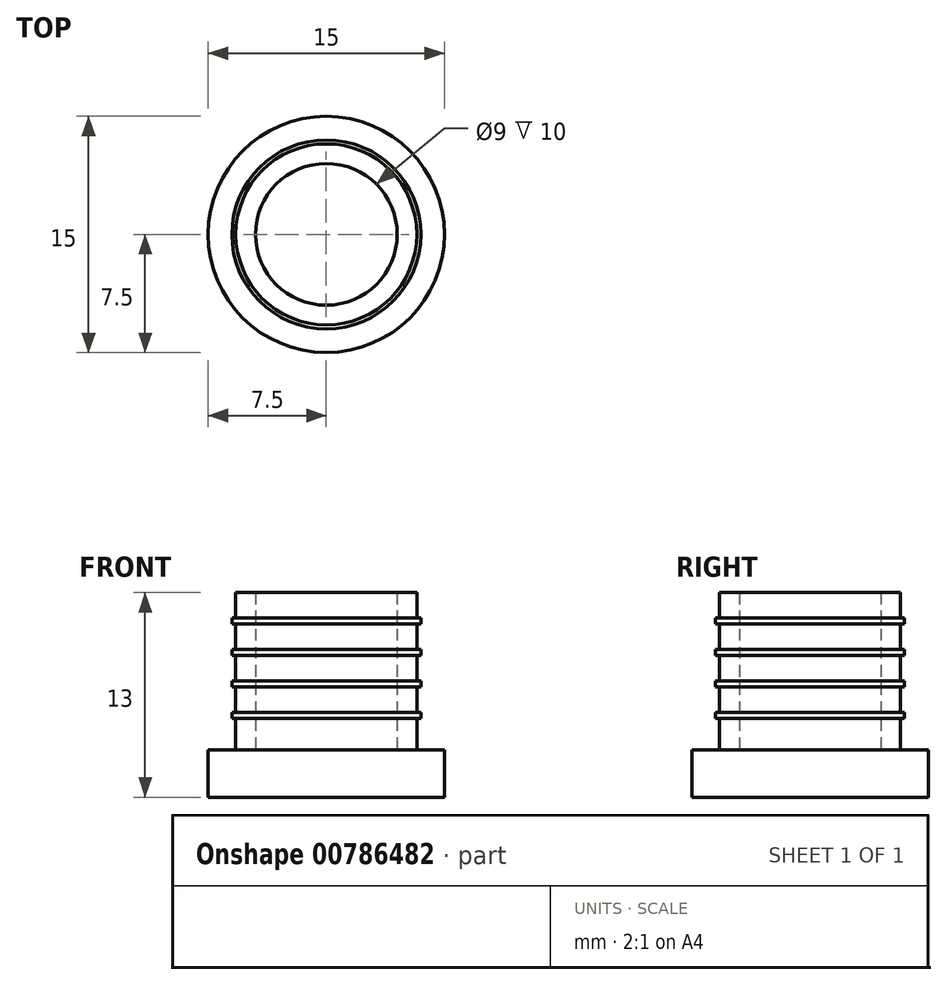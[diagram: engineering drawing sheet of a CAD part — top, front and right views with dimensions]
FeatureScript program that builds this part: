
annotation { "Feature Type Name" : "Feature", "Feature Type Description" : "" }
export const myFeature = defineFeature(function(context is Context, id is Id, definition is map)
    precondition{}
    {
        {
            var Q0;
            Q0=qCreatedBy(makeId("Top.planeOp"),FACE);
            var sketch = newSketch(context, id + "F0", { "sketchPlane" : qUnion([Q0])});
            skCircle(sketch, "E0", {"center": v(0, 0) * mm, "radius": 7.5 * mm});
            skSolve(sketch);
        }
        {
            var Q0;
            Q0 = qSketchRegion(id + "F0", true);
            extrude(context, id + "F1", {"entities" : qUnion([Q0]), "depth" : 3 * mm, "offsetDistance" : 25 * mm});
        }
        {
            var Q0;
            Q0=makeQuery(id+"F1.opExtrude","CAP_FACE",FACE,{"disambiguationData":[OSD([sQuery(id+"F0.wireOp",EDGE,"E0")])],"isStart":false});
            var sketch = newSketch(context, id + "F2", { "sketchPlane" : qUnion([Q0])});
            skCircle(sketch, "E1", {"center": v(0, 0) * mm, "radius": 5.75 * mm});
            skCircle(sketch, "E2", {"center": v(0, 0) * mm, "radius": 4.5 * mm});
            skSolve(sketch);
        }
        {
            var Q0;
            Q0 = qSketchRegion(id + "F2", true);
            extrude(context, id + "F3", {"entities" : qUnion([Q0]), "operationType" : NewBodyOperationType.ADD, "depth" : 10 * mm, "offsetDistance" : 25 * mm});
        }
        {
            var Q0;
            {var subQ0=sQuery(id+"F0.wireOp",EDGE,"E0");Q0=makeQuery(id+"F3.boolean.opBoolean","SPLIT",FACE,{"disambiguationData":[TD([makeQuery(id+"F1.opExtrude","SWEPT_FACE",FACE,{"disambiguationData":[OSD([subQ0])]})])],"derivedFrom":makeQuery(id+"F1.opExtrude","CAP_FACE",FACE,{"disambiguationData":[OSD([subQ0])],"isStart":false})});}
            cPlane(context, id + "F4", {"entities" : qUnion([Q0]), "cplaneType" : CPlaneType.OFFSET, "offset" : 2 * mm, "width" : 150 * mm, "height" : 150 * mm});
        }
        {
            var Q0;
            Q0=qCreatedBy(id+"F4.planeOp",FACE);
            var sketch = newSketch(context, id + "F5", { "sketchPlane" : qUnion([Q0])});
            skCircle(sketch, "E3", {"center": v(0, 0) * mm, "radius": 6 * mm});
            skCircle(sketch, "E4", {"center": v(0, 0) * mm, "radius": 4.5 * mm});
            skSolve(sketch);
        }
        {
            var Q0;
            Q0 = qSketchRegion(id + "F5", true);
            extrude(context, id + "F6", {"entities" : qUnion([Q0]), "operationType" : NewBodyOperationType.ADD, "depth" : 0.4 * mm, "offsetDistance" : 25 * mm});
        }
        {
            var Q0;
            Q0=qCreatedBy(id+"F4.planeOp",FACE);
            cPlane(context, id + "F7", {"entities" : qUnion([Q0]), "cplaneType" : CPlaneType.OFFSET, "offset" : 2 * mm, "width" : 150 * mm, "height" : 150 * mm});
        }
        {
            var Q0;
            Q0=qCreatedBy(id+"F7.planeOp",FACE);
            var sketch = newSketch(context, id + "F8", { "sketchPlane" : qUnion([Q0])});
            skCircle(sketch, "E5", {"center": v(0, 0) * mm, "radius": 4.5 * mm});
            skCircle(sketch, "E6", {"center": v(0, 0) * mm, "radius": 6 * mm});
            skSolve(sketch);
        }
        {
            var Q0;
            Q0 = qSketchRegion(id + "F8", true);
            extrude(context, id + "F9", {"entities" : qUnion([Q0]), "operationType" : NewBodyOperationType.ADD, "depth" : 0.4 * mm, "offsetDistance" : 25 * mm});
        }
        {
            var Q0;
            Q0=qCreatedBy(id+"F7.planeOp",FACE);
            cPlane(context, id + "F10", {"entities" : qUnion([Q0]), "cplaneType" : CPlaneType.OFFSET, "offset" : 2 * mm, "width" : 150 * mm, "height" : 150 * mm});
        }
        {
            var Q0;
            Q0=qCreatedBy(id+"F10.planeOp",FACE);
            var sketch = newSketch(context, id + "F11", { "sketchPlane" : qUnion([Q0])});
            skCircle(sketch, "E7", {"center": v(0, 0) * mm, "radius": 4.5 * mm});
            skCircle(sketch, "E8", {"center": v(0, 0) * mm, "radius": 6 * mm});
            skSolve(sketch);
        }
        {
            var Q0;
            Q0 = qSketchRegion(id + "F11", true);
            extrude(context, id + "F12", {"entities" : qUnion([Q0]), "operationType" : NewBodyOperationType.ADD, "depth" : 0.4 * mm, "offsetDistance" : 25 * mm});
        }
        {
            var Q0;
            Q0=qCreatedBy(id+"F10.planeOp",FACE);
            cPlane(context, id + "F13", {"entities" : qUnion([Q0]), "cplaneType" : CPlaneType.OFFSET, "offset" : 2 * mm, "width" : 150 * mm, "height" : 150 * mm});
        }
        {
            var Q0;
            Q0=qCreatedBy(id+"F13.planeOp",FACE);
            var sketch = newSketch(context, id + "F14", { "sketchPlane" : qUnion([Q0])});
            skCircle(sketch, "E9", {"center": v(0, 0) * mm, "radius": 4.5 * mm});
            skCircle(sketch, "E10", {"center": v(0, 0) * mm, "radius": 6 * mm});
            skSolve(sketch);
        }
        {
            var Q0;
            Q0 = qSketchRegion(id + "F14", true);
            extrude(context, id + "F15", {"entities" : qUnion([Q0]), "operationType" : NewBodyOperationType.ADD, "depth" : 0.4 * mm, "offsetDistance" : 25 * mm});
        }
    });
